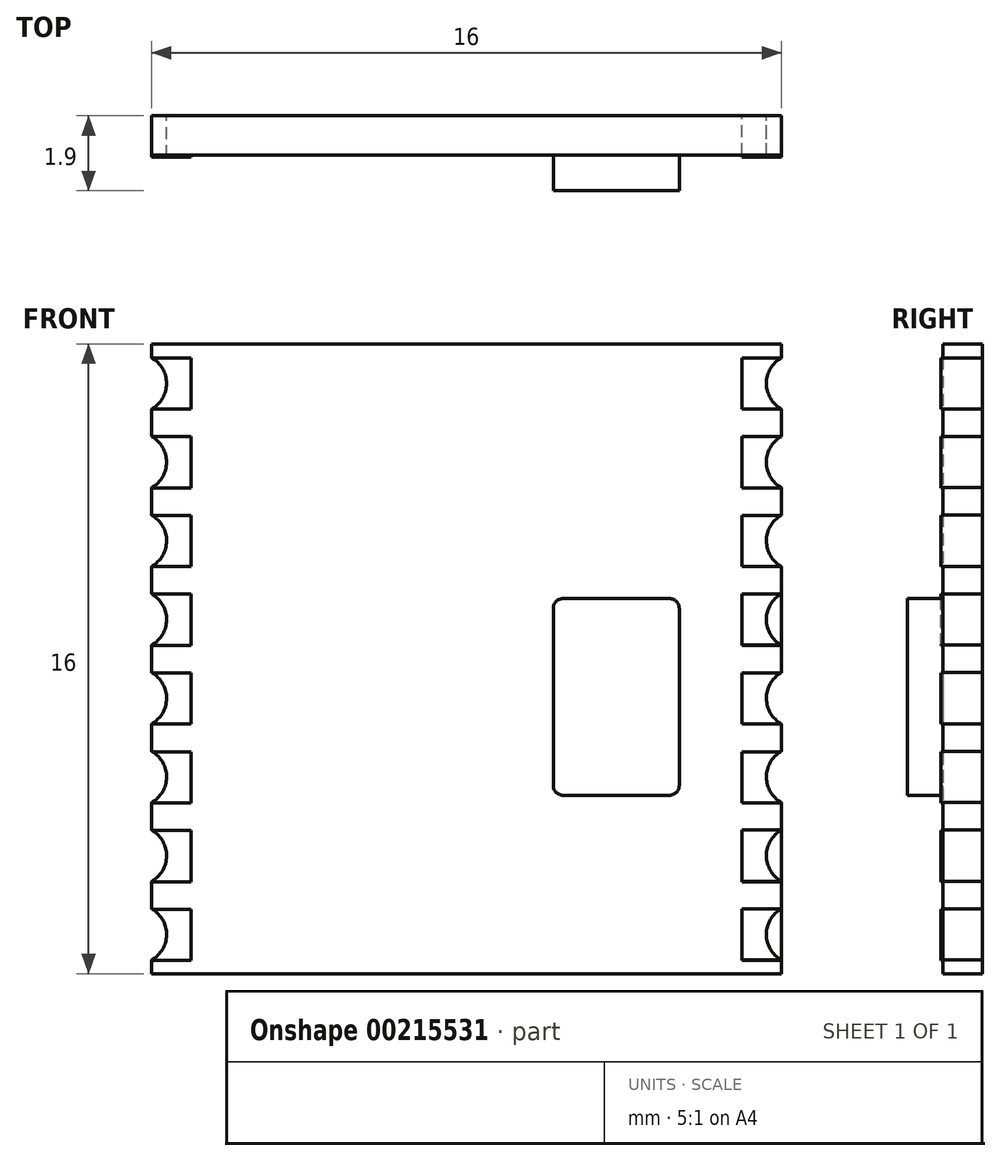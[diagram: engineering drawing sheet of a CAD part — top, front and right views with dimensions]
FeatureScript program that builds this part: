
annotation { "Feature Type Name" : "Feature", "Feature Type Description" : "" }
export const myFeature = defineFeature(function(context is Context, id is Id, definition is map)
    precondition{}
    {
        {
            var Q0;
            Q0=qCreatedBy(makeId("Front.planeOp"),FACE);
            var sketch = newSketch(context, id + "F0", { "sketchPlane" : qUnion([Q0])});
            skLineSegment(sketch, "E0.bottom", {"start": v(0, 0) * mm, "end": v(16, 0) * mm});
            skLineSegment(sketch, "E0.top", {"start": v(0, 16) * mm, "end": v(16, 16) * mm});
            skLineSegment(sketch, "E0.left", {"start": v(0, 0) * mm, "end": v(0, 16) * mm});
            skLineSegment(sketch, "E0.right", {"start": v(16, 0) * mm, "end": v(16, 16) * mm});
            skLineSegment(sketch, "E1.bottom", {"start": v(0, 15.65) * mm, "end": v(1, 15.65) * mm});
            skLineSegment(sketch, "E1.top", {"start": v(0, 14.35) * mm, "end": v(1, 14.35) * mm});
            skLineSegment(sketch, "E1.left", {"start": v(0, 15.65) * mm, "end": v(0, 14.35) * mm});
            skLineSegment(sketch, "E1.right", {"start": v(1, 15.65) * mm, "end": v(1, 14.35) * mm});
            skLineSegment(sketch, "E2", {"start": v(1, 15) * mm, "end": v(0, 15) * mm, "construction": true});
            skArc(sketch, "E3", {"start": v(0, 14.35) * mm, "mid": v(0.38, 15) * mm, "end": v(0, 15.65) * mm});
            skLineSegment(sketch, "E4", {"start": v(8, 16) * mm, "end": v(8, 0) * mm, "construction": true});
            skLineSegment(sketch, "E5.1.0.0", {"start": v(0, 12.35) * mm, "end": v(1, 12.35) * mm});
            skLineSegment(sketch, "E5.1.0.1", {"start": v(1, 13.65) * mm, "end": v(1, 12.35) * mm});
            skLineSegment(sketch, "E5.1.0.2", {"start": v(0, 13.65) * mm, "end": v(1, 13.65) * mm});
            skArc(sketch, "E5.1.0.3", {"start": v(0, 12.35) * mm, "mid": v(0.38, 13) * mm, "end": v(0, 13.65) * mm});
            skLineSegment(sketch, "E5.2.0.0", {"start": v(0, 10.35) * mm, "end": v(1, 10.35) * mm});
            skLineSegment(sketch, "E5.2.0.1", {"start": v(1, 11.65) * mm, "end": v(1, 10.35) * mm});
            skLineSegment(sketch, "E5.2.0.2", {"start": v(0, 11.65) * mm, "end": v(1, 11.65) * mm});
            skArc(sketch, "E5.2.0.3", {"start": v(0, 10.35) * mm, "mid": v(0.38, 11) * mm, "end": v(0, 11.65) * mm});
            skLineSegment(sketch, "E5.direction1", {"start": v(0, 14.35) * mm, "end": v(0, 12.35) * mm, "construction": true});
            skLineSegment(sketch, "E6.0.3.0", {"start": v(0, 8.35) * mm, "end": v(1, 8.35) * mm});
            skLineSegment(sketch, "E6.3.3.0", {"start": v(1, 9.65) * mm, "end": v(1, 8.35) * mm});
            skLineSegment(sketch, "E6.6.3.0", {"start": v(0, 9.65) * mm, "end": v(1, 9.65) * mm});
            skArc(sketch, "E6.9.3.0", {"start": v(0, 8.35) * mm, "mid": v(0.38, 9) * mm, "end": v(0, 9.65) * mm});
            skLineSegment(sketch, "E6.0.4.0", {"start": v(0, 6.35) * mm, "end": v(1, 6.35) * mm});
            skLineSegment(sketch, "E6.3.4.0", {"start": v(1, 7.65) * mm, "end": v(1, 6.35) * mm});
            skLineSegment(sketch, "E6.6.4.0", {"start": v(0, 7.65) * mm, "end": v(1, 7.65) * mm});
            skArc(sketch, "E6.9.4.0", {"start": v(0, 6.35) * mm, "mid": v(0.38, 7) * mm, "end": v(0, 7.65) * mm});
            skLineSegment(sketch, "E6.0.5.0", {"start": v(0, 4.35) * mm, "end": v(1, 4.35) * mm});
            skLineSegment(sketch, "E6.3.5.0", {"start": v(1, 5.65) * mm, "end": v(1, 4.35) * mm});
            skLineSegment(sketch, "E6.6.5.0", {"start": v(0, 5.65) * mm, "end": v(1, 5.65) * mm});
            skArc(sketch, "E6.9.5.0", {"start": v(0, 4.35) * mm, "mid": v(0.38, 5) * mm, "end": v(0, 5.65) * mm});
            skLineSegment(sketch, "E6.0.6.0", {"start": v(0, 2.35) * mm, "end": v(1, 2.35) * mm});
            skLineSegment(sketch, "E6.3.6.0", {"start": v(1, 3.65) * mm, "end": v(1, 2.35) * mm});
            skLineSegment(sketch, "E6.6.6.0", {"start": v(0, 3.65) * mm, "end": v(1, 3.65) * mm});
            skArc(sketch, "E6.9.6.0", {"start": v(0, 2.35) * mm, "mid": v(0.38, 3) * mm, "end": v(0, 3.65) * mm});
            skLineSegment(sketch, "E6.0.7.0", {"start": v(0, 0.35) * mm, "end": v(1, 0.35) * mm});
            skLineSegment(sketch, "E6.3.7.0", {"start": v(1, 1.65) * mm, "end": v(1, 0.35) * mm});
            skLineSegment(sketch, "E6.6.7.0", {"start": v(0, 1.65) * mm, "end": v(1, 1.65) * mm});
            skArc(sketch, "E6.9.7.0", {"start": v(0, 0.35) * mm, "mid": v(0.38, 1) * mm, "end": v(0, 1.65) * mm});
            skLineSegment(sketch, "E7.MirrorCS", {"start": v(16, 7.65) * mm, "end": v(15, 7.65) * mm});
            skLineSegment(sketch, "E8.MirrorCS", {"start": v(15, 15) * mm, "end": v(16, 15) * mm, "construction": true});
            skLineSegment(sketch, "E9.MirrorCS", {"start": v(15, 15.65) * mm, "end": v(15, 14.35) * mm});
            skArc(sketch, "E10.MirrorCS", {"start": v(16, 14.35) * mm, "mid": v(15.62, 15) * mm, "end": v(16, 15.65) * mm});
            skLineSegment(sketch, "E11.MirrorCS", {"start": v(16, 14.35) * mm, "end": v(16, 12.35) * mm, "construction": true});
            skLineSegment(sketch, "E12.MirrorCS", {"start": v(16, 12.35) * mm, "end": v(15, 12.35) * mm});
            skLineSegment(sketch, "E13.MirrorCS", {"start": v(15, 13.65) * mm, "end": v(15, 12.35) * mm});
            skArc(sketch, "E14.MirrorCS", {"start": v(16, 2.35) * mm, "mid": v(15.62, 3) * mm, "end": v(16, 3.65) * mm});
            skLineSegment(sketch, "E15.MirrorCS", {"start": v(16, 13.65) * mm, "end": v(15, 13.65) * mm});
            skArc(sketch, "E16.MirrorCS", {"start": v(16, 12.35) * mm, "mid": v(15.62, 13) * mm, "end": v(16, 13.65) * mm});
            skArc(sketch, "E17.MirrorCS", {"start": v(16, 6.35) * mm, "mid": v(15.62, 7) * mm, "end": v(16, 7.65) * mm});
            skLineSegment(sketch, "E18.MirrorCS", {"start": v(16, 10.35) * mm, "end": v(15, 10.35) * mm});
            skLineSegment(sketch, "E19.MirrorCS", {"start": v(16, 15.65) * mm, "end": v(16, 14.35) * mm});
            skLineSegment(sketch, "E20.MirrorCS", {"start": v(16, 14.35) * mm, "end": v(15, 14.35) * mm});
            skLineSegment(sketch, "E21.MirrorCS", {"start": v(16, 15.65) * mm, "end": v(15, 15.65) * mm});
            skArc(sketch, "E22.MirrorCS", {"start": v(16, 0.35) * mm, "mid": v(15.62, 1) * mm, "end": v(16, 1.65) * mm});
            skArc(sketch, "E23.MirrorCS", {"start": v(16, 8.35) * mm, "mid": v(15.62, 9) * mm, "end": v(16, 9.65) * mm});
            skLineSegment(sketch, "E24.MirrorCS", {"start": v(16, 8.35) * mm, "end": v(15, 8.35) * mm});
            skLineSegment(sketch, "E25.MirrorCS", {"start": v(15, 5.65) * mm, "end": v(15, 4.35) * mm});
            skLineSegment(sketch, "E26.MirrorCS", {"start": v(16, 0.35) * mm, "end": v(15, 0.35) * mm});
            skLineSegment(sketch, "E27.MirrorCS", {"start": v(15, 11.65) * mm, "end": v(15, 10.35) * mm});
            skLineSegment(sketch, "E28.MirrorCS", {"start": v(16, 2.35) * mm, "end": v(15, 2.35) * mm});
            skLineSegment(sketch, "E29.MirrorCS", {"start": v(16, 4.35) * mm, "end": v(15, 4.35) * mm});
            skLineSegment(sketch, "E30.MirrorCS", {"start": v(16, 6.35) * mm, "end": v(15, 6.35) * mm});
            skLineSegment(sketch, "E31.MirrorCS", {"start": v(15, 9.65) * mm, "end": v(15, 8.35) * mm});
            skLineSegment(sketch, "E32.MirrorCS", {"start": v(16, 5.65) * mm, "end": v(15, 5.65) * mm});
            skLineSegment(sketch, "E33.MirrorCS", {"start": v(15, 1.65) * mm, "end": v(15, 0.35) * mm});
            skLineSegment(sketch, "E34.MirrorCS", {"start": v(16, 11.65) * mm, "end": v(15, 11.65) * mm});
            skLineSegment(sketch, "E35.MirrorCS", {"start": v(15, 3.65) * mm, "end": v(15, 2.35) * mm});
            skArc(sketch, "E36.MirrorCS", {"start": v(16, 4.35) * mm, "mid": v(15.62, 5) * mm, "end": v(16, 5.65) * mm});
            skLineSegment(sketch, "E37.MirrorCS", {"start": v(16, 1.65) * mm, "end": v(15, 1.65) * mm});
            skArc(sketch, "E38.MirrorCS", {"start": v(16, 10.35) * mm, "mid": v(15.62, 11) * mm, "end": v(16, 11.65) * mm});
            skLineSegment(sketch, "E39.MirrorCS", {"start": v(16, 9.65) * mm, "end": v(15, 9.65) * mm});
            skLineSegment(sketch, "E40.MirrorCS", {"start": v(15, 7.65) * mm, "end": v(15, 6.35) * mm});
            skLineSegment(sketch, "E41.MirrorCS", {"start": v(16, 3.65) * mm, "end": v(15, 3.65) * mm});
            skSolve(sketch);
        }
        {
            var Q0;
            {var subQ18=sQuery(id+"F0.wireOp",EDGE,"E0.bottom");Q0=makeQuery(id+"F0.imprint","IMPRINT",FACE,{"disambiguationData":[TD([[makeQuery(id+"F0.imprint","IMPRINT",EDGE,{"derivedFrom":subQ18}),1.0]])]});}
            var Q1;
            Q1=makeQuery(id+"F0.imprint","IMPRINT",FACE,{"disambiguationData":[TD([[makeQuery(id+"F0.imprint","IMPRINT",EDGE,{"derivedFrom":sQuery(id+"F0.wireOp",EDGE,"E5.1.0.0")}),1.0]])]});
            var Q2;
            Q2=makeQuery(id+"F0.imprint","IMPRINT",FACE,{"disambiguationData":[TD([[makeQuery(id+"F0.imprint","IMPRINT",EDGE,{"derivedFrom":sQuery(id+"F0.wireOp",EDGE,"E5.2.0.0")}),1.0]])]});
            var Q3;
            Q3=makeQuery(id+"F0.imprint","IMPRINT",FACE,{"disambiguationData":[TD([[makeQuery(id+"F0.imprint","IMPRINT",EDGE,{"derivedFrom":sQuery(id+"F0.wireOp",EDGE,"E6.0.3.0")}),1.0]])]});
            var Q4;
            Q4=makeQuery(id+"F0.imprint","IMPRINT",FACE,{"disambiguationData":[TD([[makeQuery(id+"F0.imprint","IMPRINT",EDGE,{"derivedFrom":sQuery(id+"F0.wireOp",EDGE,"E6.0.4.0")}),1.0]])]});
            var Q5;
            Q5=makeQuery(id+"F0.imprint","IMPRINT",FACE,{"disambiguationData":[TD([[makeQuery(id+"F0.imprint","IMPRINT",EDGE,{"derivedFrom":sQuery(id+"F0.wireOp",EDGE,"E6.0.5.0")}),1.0]])]});
            var Q6;
            Q6=makeQuery(id+"F0.imprint","IMPRINT",FACE,{"disambiguationData":[TD([[makeQuery(id+"F0.imprint","IMPRINT",EDGE,{"derivedFrom":sQuery(id+"F0.wireOp",EDGE,"E6.0.6.0")}),1.0]])]});
            var Q7;
            Q7=makeQuery(id+"F0.imprint","IMPRINT",FACE,{"disambiguationData":[TD([[makeQuery(id+"F0.imprint","IMPRINT",EDGE,{"derivedFrom":sQuery(id+"F0.wireOp",EDGE,"E6.0.7.0")}),1.0]])]});
            var Q8;
            Q8=makeQuery(id+"F0.imprint","IMPRINT",FACE,{"disambiguationData":[TD([[makeQuery(id+"F0.imprint","IMPRINT",EDGE,{"derivedFrom":sQuery(id+"F0.wireOp",EDGE,"E25.MirrorCS")}),1.0]])]});
            var Q9;
            Q9=makeQuery(id+"F0.imprint","IMPRINT",FACE,{"disambiguationData":[TD([[makeQuery(id+"F0.imprint","IMPRINT",EDGE,{"derivedFrom":sQuery(id+"F0.wireOp",EDGE,"E7.MirrorCS")}),1.0]])]});
            var Q10;
            Q10=makeQuery(id+"F0.imprint","IMPRINT",FACE,{"disambiguationData":[TD([[makeQuery(id+"F0.imprint","IMPRINT",EDGE,{"derivedFrom":sQuery(id+"F0.wireOp",EDGE,"E23.MirrorCS")}),1.0]])]});
            var Q11;
            Q11=makeQuery(id+"F0.imprint","IMPRINT",FACE,{"disambiguationData":[TD([[makeQuery(id+"F0.imprint","IMPRINT",EDGE,{"derivedFrom":sQuery(id+"F0.wireOp",EDGE,"E18.MirrorCS")}),-1.0]])]});
            var Q12;
            Q12=makeQuery(id+"F0.imprint","IMPRINT",FACE,{"disambiguationData":[TD([[makeQuery(id+"F0.imprint","IMPRINT",EDGE,{"derivedFrom":sQuery(id+"F0.wireOp",EDGE,"E12.MirrorCS")}),-1.0]])]});
            var Q13;
            Q13=makeQuery(id+"F0.imprint","IMPRINT",FACE,{"disambiguationData":[TD([[makeQuery(id+"F0.imprint","IMPRINT",EDGE,{"derivedFrom":sQuery(id+"F0.wireOp",EDGE,"E9.MirrorCS")}),1.0]])]});
            var Q14;
            Q14=makeQuery(id+"F0.imprint","IMPRINT",FACE,{"disambiguationData":[TD([[makeQuery(id+"F0.imprint","IMPRINT",EDGE,{"derivedFrom":sQuery(id+"F0.wireOp",EDGE,"E14.MirrorCS")}),1.0]])]});
            var Q15;
            Q15=makeQuery(id+"F0.imprint","IMPRINT",FACE,{"disambiguationData":[TD([[makeQuery(id+"F0.imprint","IMPRINT",EDGE,{"derivedFrom":sQuery(id+"F0.wireOp",EDGE,"E22.MirrorCS")}),1.0]])]});
            var Q16;
            Q16=makeQuery(id+"F0.imprint","IMPRINT",FACE,{"disambiguationData":[TD([[makeQuery(id+"F0.imprint","IMPRINT",EDGE,{"derivedFrom":sQuery(id+"F0.wireOp",EDGE,"E1.bottom")}),-1.0]])]});
            extrude(context, id + "F1", {"entities" : qUnion([Q0, Q1, Q2, Q3, Q4, Q5, Q6, Q7, Q8, Q9, Q10, Q11, Q12, Q13, Q14, Q15, Q16]), "depth" : 1 * mm});
        }
        {
            var Q0;
            Q0=makeQuery(id+"F1.opExtrude","CAP_FACE",FACE,{"disambiguationData":[OSD([sQuery(id+"F0.wireOp",EDGE,"E0.bottom"),sQuery(id+"F0.wireOp",EDGE,"E0.top"),sQuery(id+"F0.wireOp",EDGE,"E0.left"),sQuery(id+"F0.wireOp",EDGE,"E3"),sQuery(id+"F0.wireOp",EDGE,"E5.1.0.3"),sQuery(id+"F0.wireOp",EDGE,"E5.2.0.3"),sQuery(id+"F0.wireOp",EDGE,"E6.9.3.0"),sQuery(id+"F0.wireOp",EDGE,"E6.9.4.0"),sQuery(id+"F0.wireOp",EDGE,"E6.9.5.0"),sQuery(id+"F0.wireOp",EDGE,"E6.9.6.0"),sQuery(id+"F0.wireOp",EDGE,"E6.9.7.0"),sQuery(id+"F0.wireOp",EDGE,"E10.MirrorCS"),sQuery(id+"F0.wireOp",EDGE,"E14.MirrorCS"),sQuery(id+"F0.wireOp",EDGE,"E16.MirrorCS"),sQuery(id+"F0.wireOp",EDGE,"E17.MirrorCS"),sQuery(id+"F0.wireOp",EDGE,"E0.right"),sQuery(id+"F0.wireOp",EDGE,"E22.MirrorCS"),sQuery(id+"F0.wireOp",EDGE,"E23.MirrorCS"),sQuery(id+"F0.wireOp",EDGE,"E36.MirrorCS"),sQuery(id+"F0.wireOp",EDGE,"E38.MirrorCS")])],"isStart":false});
            var sketch = newSketch(context, id + "F2", { "sketchPlane" : qUnion([Q0])});
            skLineSegment(sketch, "E42", {"start": v(0, 15.65) * mm, "end": v(1, 15.65) * mm});
            skLineSegment(sketch, "E43", {"start": v(1, 15.65) * mm, "end": v(1, 14.35) * mm});
            skLineSegment(sketch, "E44", {"start": v(1, 14.35) * mm, "end": v(0, 14.35) * mm});
            skLineSegment(sketch, "E45.1.0.0", {"start": v(1, 12.35) * mm, "end": v(0, 12.35) * mm});
            skLineSegment(sketch, "E45.1.0.1", {"start": v(1, 13.65) * mm, "end": v(1, 12.35) * mm});
            skLineSegment(sketch, "E45.1.0.2", {"start": v(0, 13.65) * mm, "end": v(1, 13.65) * mm});
            skLineSegment(sketch, "E45.2.0.0", {"start": v(1, 10.35) * mm, "end": v(0, 10.35) * mm});
            skLineSegment(sketch, "E45.2.0.1", {"start": v(1, 11.65) * mm, "end": v(1, 10.35) * mm});
            skLineSegment(sketch, "E45.2.0.2", {"start": v(0, 11.65) * mm, "end": v(1, 11.65) * mm});
            skLineSegment(sketch, "E45.direction1", {"start": v(0, 14.35) * mm, "end": v(0, 12.35) * mm, "construction": true});
            skLineSegment(sketch, "E46.0.3.0", {"start": v(1, 8.34) * mm, "end": v(0, 8.34) * mm});
            skLineSegment(sketch, "E46.3.3.0", {"start": v(1, 9.64) * mm, "end": v(1, 8.34) * mm});
            skLineSegment(sketch, "E46.6.3.0", {"start": v(0, 9.64) * mm, "end": v(1, 9.64) * mm});
            skLineSegment(sketch, "E46.0.4.0", {"start": v(1, 6.34) * mm, "end": v(0, 6.34) * mm});
            skLineSegment(sketch, "E46.3.4.0", {"start": v(1, 7.64) * mm, "end": v(1, 6.34) * mm});
            skLineSegment(sketch, "E46.6.4.0", {"start": v(0, 7.64) * mm, "end": v(1, 7.64) * mm});
            skLineSegment(sketch, "E46.0.5.0", {"start": v(1, 4.34) * mm, "end": v(0, 4.34) * mm});
            skLineSegment(sketch, "E46.3.5.0", {"start": v(1, 5.64) * mm, "end": v(1, 4.34) * mm});
            skLineSegment(sketch, "E46.6.5.0", {"start": v(0, 5.64) * mm, "end": v(1, 5.64) * mm});
            skLineSegment(sketch, "E46.0.6.0", {"start": v(1, 2.34) * mm, "end": v(0, 2.34) * mm});
            skLineSegment(sketch, "E46.3.6.0", {"start": v(1, 3.64) * mm, "end": v(1, 2.34) * mm});
            skLineSegment(sketch, "E46.6.6.0", {"start": v(0, 3.64) * mm, "end": v(1, 3.64) * mm});
            skLineSegment(sketch, "E46.0.7.0", {"start": v(1, 0.34) * mm, "end": v(0, 0.34) * mm});
            skLineSegment(sketch, "E46.3.7.0", {"start": v(1, 1.64) * mm, "end": v(1, 0.34) * mm});
            skLineSegment(sketch, "E46.6.7.0", {"start": v(0, 1.64) * mm, "end": v(1, 1.64) * mm});
            skLineSegment(sketch, "E47", {"start": v(8, 16) * mm, "end": v(8, 0) * mm, "construction": true});
            skLineSegment(sketch, "E48.MirrorCS", {"start": v(15, 3.64) * mm, "end": v(15, 2.34) * mm});
            skLineSegment(sketch, "E49.MirrorCS", {"start": v(15, 2.34) * mm, "end": v(16, 2.34) * mm});
            skLineSegment(sketch, "E50.MirrorCS", {"start": v(16, 5.64) * mm, "end": v(15, 5.64) * mm});
            skLineSegment(sketch, "E51.MirrorCS", {"start": v(15, 0.34) * mm, "end": v(16, 0.34) * mm});
            skLineSegment(sketch, "E52.MirrorCS", {"start": v(16, 9.64) * mm, "end": v(15, 9.64) * mm});
            skLineSegment(sketch, "E53.MirrorCS", {"start": v(15, 9.64) * mm, "end": v(15, 8.34) * mm});
            skLineSegment(sketch, "E54.MirrorCS", {"start": v(15, 8.34) * mm, "end": v(16, 8.34) * mm});
            skLineSegment(sketch, "E55.MirrorCS", {"start": v(16, 14.35) * mm, "end": v(16, 12.35) * mm, "construction": true});
            skLineSegment(sketch, "E56.MirrorCS", {"start": v(16, 11.65) * mm, "end": v(15, 11.65) * mm});
            skLineSegment(sketch, "E57.MirrorCS", {"start": v(15, 11.65) * mm, "end": v(15, 10.35) * mm});
            skLineSegment(sketch, "E58.MirrorCS", {"start": v(15, 10.35) * mm, "end": v(16, 10.35) * mm});
            skLineSegment(sketch, "E59.MirrorCS", {"start": v(16, 13.65) * mm, "end": v(15, 13.65) * mm});
            skLineSegment(sketch, "E60.MirrorCS", {"start": v(15, 13.65) * mm, "end": v(15, 12.35) * mm});
            skLineSegment(sketch, "E61.MirrorCS", {"start": v(15, 12.35) * mm, "end": v(16, 12.35) * mm});
            skLineSegment(sketch, "E62.MirrorCS", {"start": v(15, 14.35) * mm, "end": v(16, 14.35) * mm});
            skLineSegment(sketch, "E63.MirrorCS", {"start": v(15, 5.64) * mm, "end": v(15, 4.34) * mm});
            skLineSegment(sketch, "E64.MirrorCS", {"start": v(15, 6.34) * mm, "end": v(16, 6.34) * mm});
            skLineSegment(sketch, "E65.MirrorCS", {"start": v(15, 7.64) * mm, "end": v(15, 6.34) * mm});
            skLineSegment(sketch, "E66.MirrorCS", {"start": v(16, 7.64) * mm, "end": v(15, 7.64) * mm});
            skLineSegment(sketch, "E67.MirrorCS", {"start": v(16, 15.65) * mm, "end": v(15, 15.65) * mm});
            skLineSegment(sketch, "E68.MirrorCS", {"start": v(15, 15.65) * mm, "end": v(15, 14.35) * mm});
            skLineSegment(sketch, "E69.MirrorCS", {"start": v(15, 4.34) * mm, "end": v(16, 4.34) * mm});
            skLineSegment(sketch, "E70.MirrorCS", {"start": v(16, 1.64) * mm, "end": v(15, 1.64) * mm});
            skLineSegment(sketch, "E71.MirrorCS", {"start": v(16, 3.64) * mm, "end": v(15, 3.64) * mm});
            skLineSegment(sketch, "E72.MirrorCS", {"start": v(15, 1.64) * mm, "end": v(15, 0.34) * mm});
            skSolve(sketch);
        }
        {
            var Q0;
            Q0=makeQuery(id+"F2.imprint","IMPRINT",FACE,{"disambiguationData":[TD([[makeQuery(id+"F2.imprint","IMPRINT",EDGE,{"derivedFrom":sQuery(id+"F2.wireOp",EDGE,"E62.MirrorCS")}),1.0]])]});
            var Q1;
            {var subQ7=sQuery(id+"F2.wireOp",EDGE,"E60.MirrorCS");Q1=makeQuery(id+"F2.imprint","IMPRINT",FACE,{"disambiguationData":[TD([[makeQuery(id+"F2.imprint","IMPRINT",EDGE,{"derivedFrom":subQ7}),1.0]])]});}
            var Q2;
            {var subQ8=sQuery(id+"F2.wireOp",EDGE,"E57.MirrorCS");Q2=makeQuery(id+"F2.imprint","IMPRINT",FACE,{"disambiguationData":[TD([[makeQuery(id+"F2.imprint","IMPRINT",EDGE,{"derivedFrom":subQ8}),1.0]])]});}
            var Q3;
            {var subQ6=sQuery(id+"F2.wireOp",EDGE,"E53.MirrorCS");Q3=makeQuery(id+"F2.imprint","IMPRINT",FACE,{"disambiguationData":[TD([[makeQuery(id+"F2.imprint","IMPRINT",EDGE,{"derivedFrom":subQ6}),1.0]])]});}
            var Q4;
            {var subQ8=sQuery(id+"F2.wireOp",EDGE,"E64.MirrorCS");Q4=makeQuery(id+"F2.imprint","IMPRINT",FACE,{"disambiguationData":[TD([[makeQuery(id+"F2.imprint","IMPRINT",EDGE,{"derivedFrom":subQ8}),1.0]])]});}
            var Q5;
            {var subQ6=sQuery(id+"F2.wireOp",EDGE,"E63.MirrorCS");Q5=makeQuery(id+"F2.imprint","IMPRINT",FACE,{"disambiguationData":[TD([[makeQuery(id+"F2.imprint","IMPRINT",EDGE,{"derivedFrom":subQ6}),1.0]])]});}
            var Q6;
            {var subQ1=sQuery(id+"F2.wireOp",EDGE,"E48.MirrorCS");Q6=makeQuery(id+"F2.imprint","IMPRINT",FACE,{"disambiguationData":[TD([[makeQuery(id+"F2.imprint","IMPRINT",EDGE,{"derivedFrom":subQ1}),1.0]])]});}
            var Q7;
            {var subQ8=sQuery(id+"F2.wireOp",EDGE,"E51.MirrorCS");Q7=makeQuery(id+"F2.imprint","IMPRINT",FACE,{"disambiguationData":[TD([[makeQuery(id+"F2.imprint","IMPRINT",EDGE,{"derivedFrom":subQ8}),1.0]])]});}
            var Q8;
            {var subQ8=sQuery(id+"F2.wireOp",EDGE,"E46.0.7.0");Q8=makeQuery(id+"F2.imprint","IMPRINT",FACE,{"disambiguationData":[TD([[makeQuery(id+"F2.imprint","IMPRINT",EDGE,{"derivedFrom":subQ8}),-1.0]])]});}
            var Q9;
            {var subQ5=sQuery(id+"F2.wireOp",EDGE,"E46.0.6.0");Q9=makeQuery(id+"F2.imprint","IMPRINT",FACE,{"disambiguationData":[TD([[makeQuery(id+"F2.imprint","IMPRINT",EDGE,{"derivedFrom":subQ5}),-1.0]])]});}
            var Q10;
            {var subQ5=sQuery(id+"F2.wireOp",EDGE,"E46.0.5.0");Q10=makeQuery(id+"F2.imprint","IMPRINT",FACE,{"disambiguationData":[TD([[makeQuery(id+"F2.imprint","IMPRINT",EDGE,{"derivedFrom":subQ5}),-1.0]])]});}
            var Q11;
            {var subQ5=sQuery(id+"F2.wireOp",EDGE,"E46.0.4.0");Q11=makeQuery(id+"F2.imprint","IMPRINT",FACE,{"disambiguationData":[TD([[makeQuery(id+"F2.imprint","IMPRINT",EDGE,{"derivedFrom":subQ5}),-1.0]])]});}
            var Q12;
            {var subQ5=sQuery(id+"F2.wireOp",EDGE,"E46.0.3.0");Q12=makeQuery(id+"F2.imprint","IMPRINT",FACE,{"disambiguationData":[TD([[makeQuery(id+"F2.imprint","IMPRINT",EDGE,{"derivedFrom":subQ5}),-1.0]])]});}
            var Q13;
            {var subQ8=sQuery(id+"F2.wireOp",EDGE,"E45.2.0.0");Q13=makeQuery(id+"F2.imprint","IMPRINT",FACE,{"disambiguationData":[TD([[makeQuery(id+"F2.imprint","IMPRINT",EDGE,{"derivedFrom":subQ8}),-1.0]])]});}
            var Q14;
            {var subQ5=sQuery(id+"F2.wireOp",EDGE,"E45.1.0.0");Q14=makeQuery(id+"F2.imprint","IMPRINT",FACE,{"disambiguationData":[TD([[makeQuery(id+"F2.imprint","IMPRINT",EDGE,{"derivedFrom":subQ5}),-1.0]])]});}
            var Q15;
            Q15=makeQuery(id+"F2.imprint","IMPRINT",FACE,{"disambiguationData":[TD([[makeQuery(id+"F2.imprint","IMPRINT",EDGE,{"derivedFrom":sQuery(id+"F2.wireOp",EDGE,"E42")}),-1.0]])]});
            extrude(context, id + "F3", {"entities" : qUnion([Q0, Q1, Q2, Q3, Q4, Q5, Q6, Q7, Q8, Q9, Q10, Q11, Q12, Q13, Q14, Q15]), "operationType" : NewBodyOperationType.ADD, "depth" : 0.05 * mm});
        }
        {
            var Q0;
            Q0=makeQuery(id+"F1.opExtrude","CAP_FACE",FACE,{"disambiguationData":[OSD([sQuery(id+"F0.wireOp",EDGE,"E0.bottom"),sQuery(id+"F0.wireOp",EDGE,"E0.top"),sQuery(id+"F0.wireOp",EDGE,"E0.left"),sQuery(id+"F0.wireOp",EDGE,"E3"),sQuery(id+"F0.wireOp",EDGE,"E5.1.0.3"),sQuery(id+"F0.wireOp",EDGE,"E5.2.0.3"),sQuery(id+"F0.wireOp",EDGE,"E6.9.3.0"),sQuery(id+"F0.wireOp",EDGE,"E6.9.4.0"),sQuery(id+"F0.wireOp",EDGE,"E6.9.5.0"),sQuery(id+"F0.wireOp",EDGE,"E6.9.6.0"),sQuery(id+"F0.wireOp",EDGE,"E6.9.7.0"),sQuery(id+"F0.wireOp",EDGE,"E10.MirrorCS"),sQuery(id+"F0.wireOp",EDGE,"E14.MirrorCS"),sQuery(id+"F0.wireOp",EDGE,"E16.MirrorCS"),sQuery(id+"F0.wireOp",EDGE,"E17.MirrorCS"),sQuery(id+"F0.wireOp",EDGE,"E0.right"),sQuery(id+"F0.wireOp",EDGE,"E22.MirrorCS"),sQuery(id+"F0.wireOp",EDGE,"E23.MirrorCS"),sQuery(id+"F0.wireOp",EDGE,"E36.MirrorCS"),sQuery(id+"F0.wireOp",EDGE,"E38.MirrorCS")])],"isStart":false});
            var sketch = newSketch(context, id + "F4", { "sketchPlane" : qUnion([Q0])});
            skLineSegment(sketch, "E73.bottom", {"start": v(10.2, 9.53) * mm, "end": v(13.4, 9.53) * mm});
            skLineSegment(sketch, "E73.top", {"start": v(10.2, 4.53) * mm, "end": v(13.4, 4.53) * mm});
            skLineSegment(sketch, "E73.left", {"start": v(10.2, 9.53) * mm, "end": v(10.2, 4.53) * mm});
            skLineSegment(sketch, "E73.right", {"start": v(13.4, 9.53) * mm, "end": v(13.4, 4.53) * mm});
            skSolve(sketch);
        }
        {
            var Q0;
            Q0=makeQuery(id+"F4.imprint","IMPRINT",FACE,{"disambiguationData":[TD([[makeQuery(id+"F4.imprint","IMPRINT",EDGE,{"derivedFrom":sQuery(id+"F4.wireOp",EDGE,"E73.bottom")}),-1.0]])]});
            extrude(context, id + "F5", {"entities" : qUnion([Q0]), "operationType" : NewBodyOperationType.ADD, "depth" : 0.9 * mm});
        }
        {
            var Q0;
            Q0=makeQuery(id+"F5.opExtrude","SWEPT_EDGE",EDGE,{"disambiguationData":[OSD([sQuery(id+"F4.wireOp",EDGE,"E73.top"),sQuery(id+"F4.wireOp",EDGE,"E73.left")])]});
            var Q1;
            Q1=makeQuery(id+"F5.opExtrude","SWEPT_EDGE",EDGE,{"disambiguationData":[OSD([sQuery(id+"F4.wireOp",EDGE,"E73.top"),sQuery(id+"F4.wireOp",EDGE,"E73.right")])]});
            var Q2;
            Q2=makeQuery(id+"F5.opExtrude","SWEPT_EDGE",EDGE,{"disambiguationData":[OSD([sQuery(id+"F4.wireOp",EDGE,"E73.bottom"),sQuery(id+"F4.wireOp",EDGE,"E73.left")])]});
            var Q3;
            Q3=makeQuery(id+"F5.opExtrude","SWEPT_EDGE",EDGE,{"disambiguationData":[OSD([sQuery(id+"F4.wireOp",EDGE,"E73.bottom"),sQuery(id+"F4.wireOp",EDGE,"E73.right")])]});
            fillet(context, id + "F6", {"entities" : qUnion([Q0, Q1, Q2, Q3]), "radius" : 0.25 * mm, "tangentPropagation" : true, "allowEdgeOverflow" : false});
        }
    });
